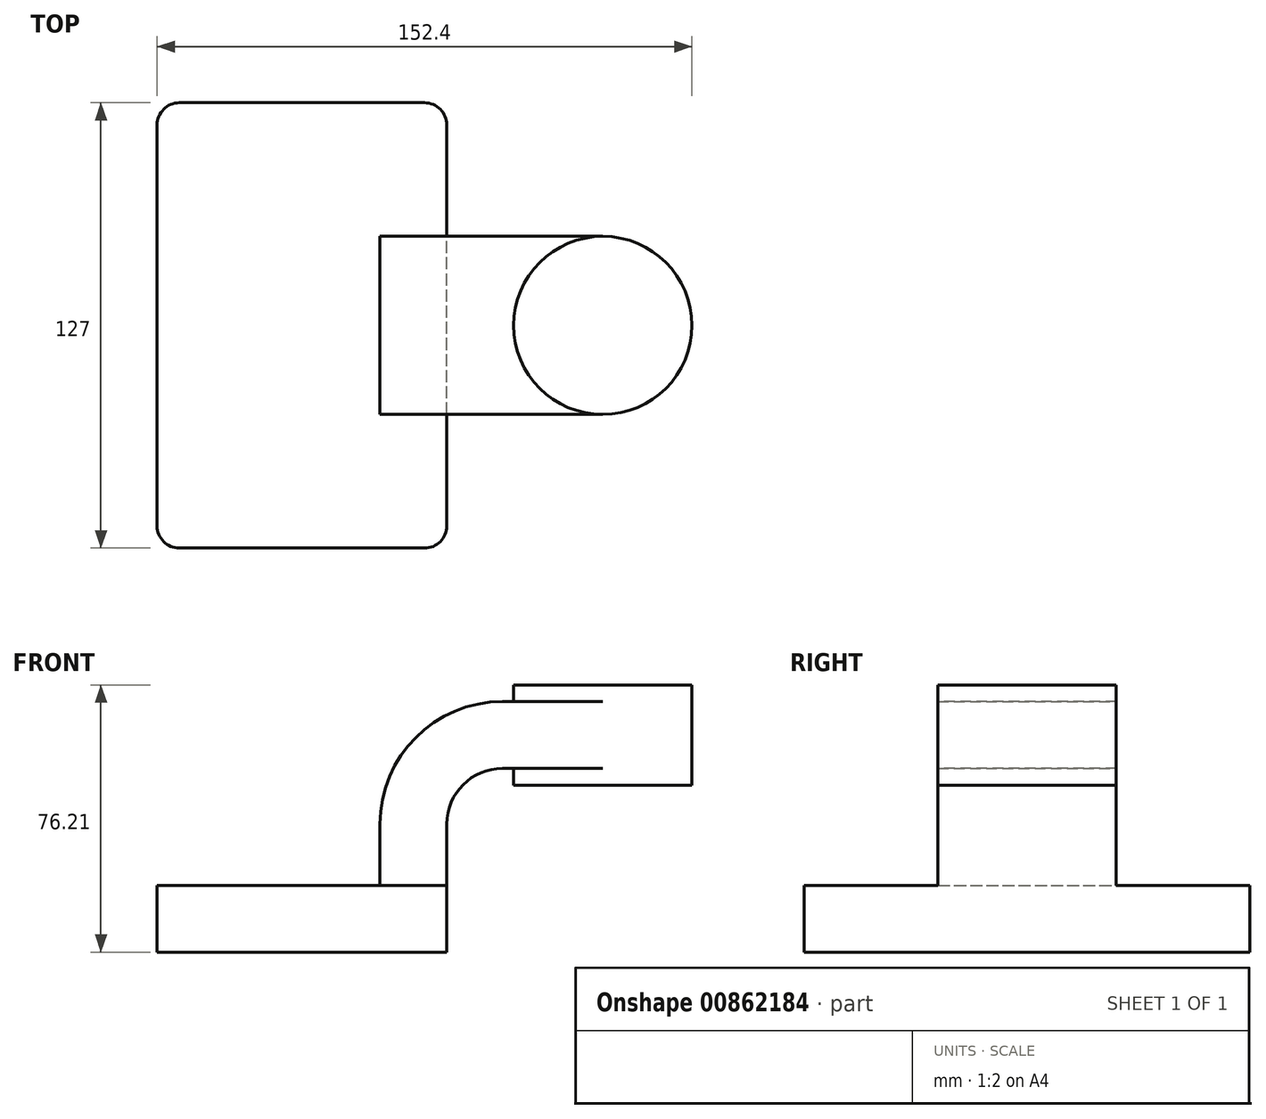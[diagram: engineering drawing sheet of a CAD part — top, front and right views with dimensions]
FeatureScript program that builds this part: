
annotation { "Feature Type Name" : "Feature", "Feature Type Description" : "" }
export const myFeature = defineFeature(function(context is Context, id is Id, definition is map)
    precondition{}
    {
        {
            var Q0;
            Q0=qCreatedBy(makeId("Front.planeOp"),FACE);
            var sketch = newSketch(context, id + "F0", { "sketchPlane" : qUnion([Q0])});
            skLineSegment(sketch, "E0.bottom", {"start": v(41.28, -9.52) * mm, "end": v(-41.28, -9.53) * mm});
            skLineSegment(sketch, "E0.top", {"start": v(41.28, 9.53) * mm, "end": v(-41.28, 9.52) * mm});
            skLineSegment(sketch, "E0.left", {"start": v(41.28, -9.52) * mm, "end": v(41.28, 9.53) * mm});
            skLineSegment(sketch, "E0.right", {"start": v(-41.28, -9.53) * mm, "end": v(-41.28, 9.52) * mm});
            skPoint(sketch, "E0.middle", {"position": v(0, 0) * mm});
            skLineSegment(sketch, "E1.bottom", {"start": v(111.12, 38.1) * mm, "end": v(60.32, 38.1) * mm});
            skLineSegment(sketch, "E1.top", {"start": v(111.12, 66.68) * mm, "end": v(60.32, 66.68) * mm});
            skLineSegment(sketch, "E1.left", {"start": v(111.12, 38.1) * mm, "end": v(111.12, 66.68) * mm});
            skLineSegment(sketch, "E1.right", {"start": v(60.32, 38.1) * mm, "end": v(60.32, 66.68) * mm});
            skPoint(sketch, "E1.middle", {"position": v(85.72, 52.39) * mm});
            skLineSegment(sketch, "E2", {"start": v(41.28, 9.53) * mm, "end": v(41.28, 26.99) * mm});
            skArc(sketch, "E3", {"start": v(41.28, 26.99) * mm, "mid": v(45.92, 38.21) * mm, "end": v(57.15, 42.86) * mm});
            skLineSegment(sketch, "E4", {"start": v(57.15, 42.86) * mm, "end": v(85.73, 42.86) * mm});
            skLineSegment(sketch, "E5.0", {"start": v(57.15, 61.91) * mm, "end": v(85.73, 61.91) * mm});
            skArc(sketch, "E5.1", {"start": v(22.23, 26.99) * mm, "mid": v(32.45, 51.68) * mm, "end": v(57.15, 61.91) * mm});
            skLineSegment(sketch, "E5.2", {"start": v(22.23, 9.53) * mm, "end": v(22.23, 26.99) * mm});
            skFitSpline(sketch, "E6", {"points": [v(-41.28, 9.52) * mm, v(57.15, 61.91) * mm], "startDerivative": vector(0, 110.74) * mm, "endDerivative": vector(171.45, 0) * mm});
            skLineSegment(sketch, "E7", {"start": v(85.72, 66.68) * mm, "end": v(85.72, 38.1) * mm});
            skSolve(sketch);
        }
        {
            var Q0;
            Q0=makeQuery(id+"F0.imprint","IMPRINT",FACE,{"disambiguationData":[TD([[makeQuery(id+"F0.imprint","IMPRINT",EDGE,{"derivedFrom":sQuery(id+"F0.wireOp",EDGE,"E0.bottom")}),-1.0]])]});
            extrude(context, id + "F1", {"entities" : qUnion([Q0]), "endBound" : BoundingType.SYMMETRIC, "depth" : 127 * mm, "offsetDistance" : 25.4 * mm});
        }
        {
            var Q0;
            {var subQ1=sQuery(id+"F0.wireOp",EDGE,"E2");Q0=makeQuery(id+"F0.imprint","IMPRINT",FACE,{"disambiguationData":[TD([[makeQuery(id+"F0.imprint","IMPRINT",EDGE,{"derivedFrom":subQ1}),1.0]])]});}
            var Q1;
            {var subQ5=sQuery(id+"F0.wireOp",EDGE,"RSQgiEi3-IMnr-pycF-dPir-vu3G25fSJynE");Q1=makeQuery(id+"F0.imprint","IMPRINT",FACE,{"disambiguationData":[TD([[makeQuery(id+"F0.imprint","IMPRINT",EDGE,{"derivedFrom":subQ5}),-1.0]])]});}
            var Q2;
            {var subQ0=sQuery(id+"F0.wireOp",EDGE,"E4");var subQ1=sQuery(id+"F0.wireOp",EDGE,"E1.right");var subQ2=makeQuery(id+"F0.imprint","INTERSECT",VERTEX,{"derivedFrom":[subQ1,subQ0]});Q2=makeQuery(id+"F0.imprint","IMPRINT",FACE,{"disambiguationData":[TD([[makeQuery(id+"F0.imprint","IMPRINT",EDGE,{"disambiguationData":[TD([[subQ2,-1.0]])],"derivedFrom":subQ1}),-1.0]])]});}
            extrude(context, id + "F2", {"entities" : qUnion([Q0, Q1, Q2]), "operationType" : NewBodyOperationType.ADD, "endBound" : BoundingType.SYMMETRIC, "depth" : 50.8 * mm, "offsetDistance" : 25.4 * mm});
        }
        {
            var Q0;
            Q0=makeQuery(id+"F0.imprint","IMPRINT",FACE,{"disambiguationData":[TD([[makeQuery(id+"F0.imprint","IMPRINT",EDGE,{"derivedFrom":sQuery(id+"F0.wireOp",EDGE,"E5.1")}),1.0]])]});
            extrude(context, id + "F3", {"entities" : qUnion([Q0]), "operationType" : NewBodyOperationType.ADD, "endBound" : BoundingType.SYMMETRIC, "depth" : 15.88 * mm, "offsetDistance" : 25.4 * mm});
        }
        {
            var Q0;
            {var subQ0=sQuery(id+"F0.wireOp",EDGE,"E1.left");Q0=makeQuery(id+"F0.imprint","IMPRINT",FACE,{"disambiguationData":[TD([[makeQuery(id+"F0.imprint","IMPRINT",EDGE,{"derivedFrom":subQ0}),1.0]])]});}
            var Q1;
            Q1=sQuery(id+"F0.wireOp",EDGE,"E7");
            revolve(context, id + "F4", {"operationType" : NewBodyOperationType.ADD, "surfaceOperationType" : NewSurfaceOperationType.NEW, "entities" : qUnion([Q0]), "axis" : qUnion([Q1]), "revolveType" : RevolveType.FULL});
        }
        {
            var Q0;
            Q0=makeQuery(id+"F1.opExtrude","CAP_EDGE",EDGE,{"disambiguationData":[OSD([sQuery(id+"F0.wireOp",EDGE,"E0.left")])],"isStart":false});
            var Q1;
            Q1=makeQuery(id+"F1.opExtrude","CAP_EDGE",EDGE,{"disambiguationData":[OSD([sQuery(id+"F0.wireOp",EDGE,"E0.left")])],"isStart":true});
            var Q2;
            Q2=makeQuery(id+"F1.opExtrude","CAP_EDGE",EDGE,{"disambiguationData":[OSD([sQuery(id+"F0.wireOp",EDGE,"E0.right")])],"isStart":true});
            var Q3;
            Q3=makeQuery(id+"F1.opExtrude","CAP_EDGE",EDGE,{"disambiguationData":[OSD([sQuery(id+"F0.wireOp",EDGE,"E0.right")])],"isStart":false});
            fillet(context, id + "F5", {"entities" : qUnion([Q0, Q1, Q2, Q3]), "radius" : 6.35 * mm, "tangentPropagation" : true, "allowEdgeOverflow" : false});
        }
    });
